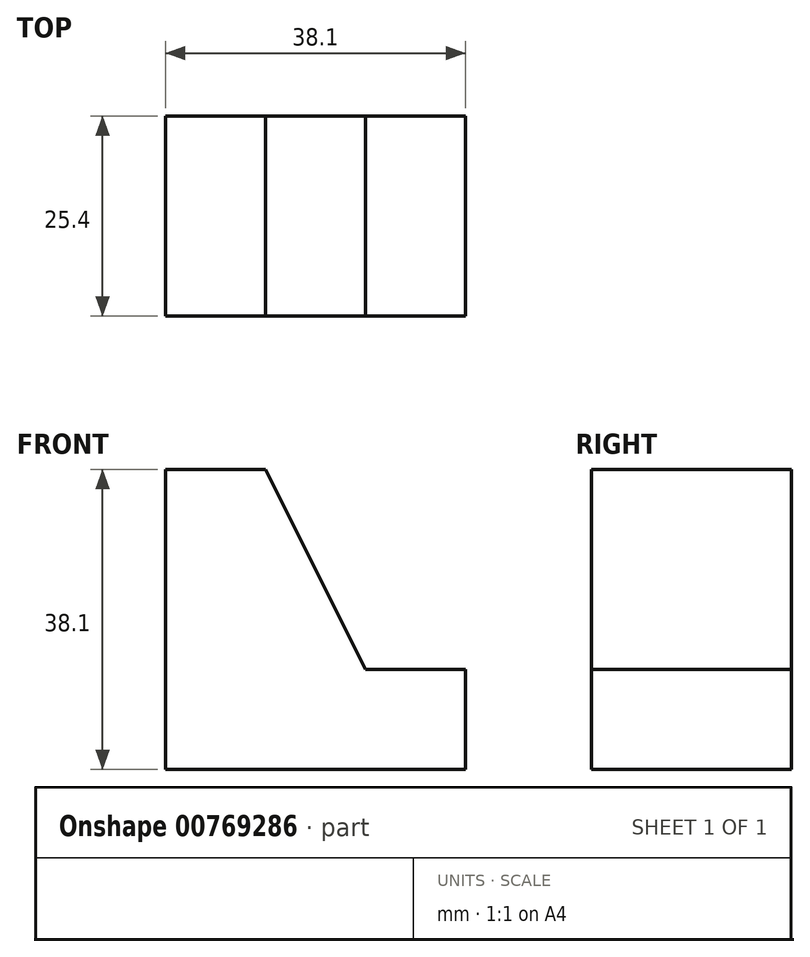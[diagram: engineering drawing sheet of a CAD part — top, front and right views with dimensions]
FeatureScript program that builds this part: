
annotation { "Feature Type Name" : "Feature", "Feature Type Description" : "" }
export const myFeature = defineFeature(function(context is Context, id is Id, definition is map)
    precondition{}
    {
        {
            var Q0;
            Q0=qCreatedBy(makeId("Front.planeOp"),FACE);
            var sketch = newSketch(context, id + "F0", { "sketchPlane" : qUnion([Q0])});
            skLineSegment(sketch, "E0", {"start": v(0, 0) * mm, "end": v(38.1, 0) * mm});
            skLineSegment(sketch, "E1", {"start": v(38.1, 0) * mm, "end": v(38.1, 12.7) * mm});
            skLineSegment(sketch, "E2", {"start": v(38.1, 12.7) * mm, "end": v(25.4, 12.7) * mm});
            skLineSegment(sketch, "E3", {"start": v(0, 0) * mm, "end": v(0, 38.1) * mm});
            skLineSegment(sketch, "E4", {"start": v(0, 38.1) * mm, "end": v(12.7, 38.1) * mm});
            skLineSegment(sketch, "E5", {"start": v(12.7, 38.1) * mm, "end": v(25.4, 12.7) * mm});
            skSolve(sketch);
        }
        {
            var Q0;
            Q0=makeQuery(id+"F0.imprint","IMPRINT",FACE,{"disambiguationData":[TD([[makeQuery(id+"F0.imprint","IMPRINT",EDGE,{"derivedFrom":sQuery(id+"F0.wireOp",EDGE,"E0")}),1.0]])]});
            extrude(context, id + "F1", {"entities" : qUnion([Q0]), "depth" : 25.4 * mm, "offsetDistance" : 25.4 * mm});
        }
    });
